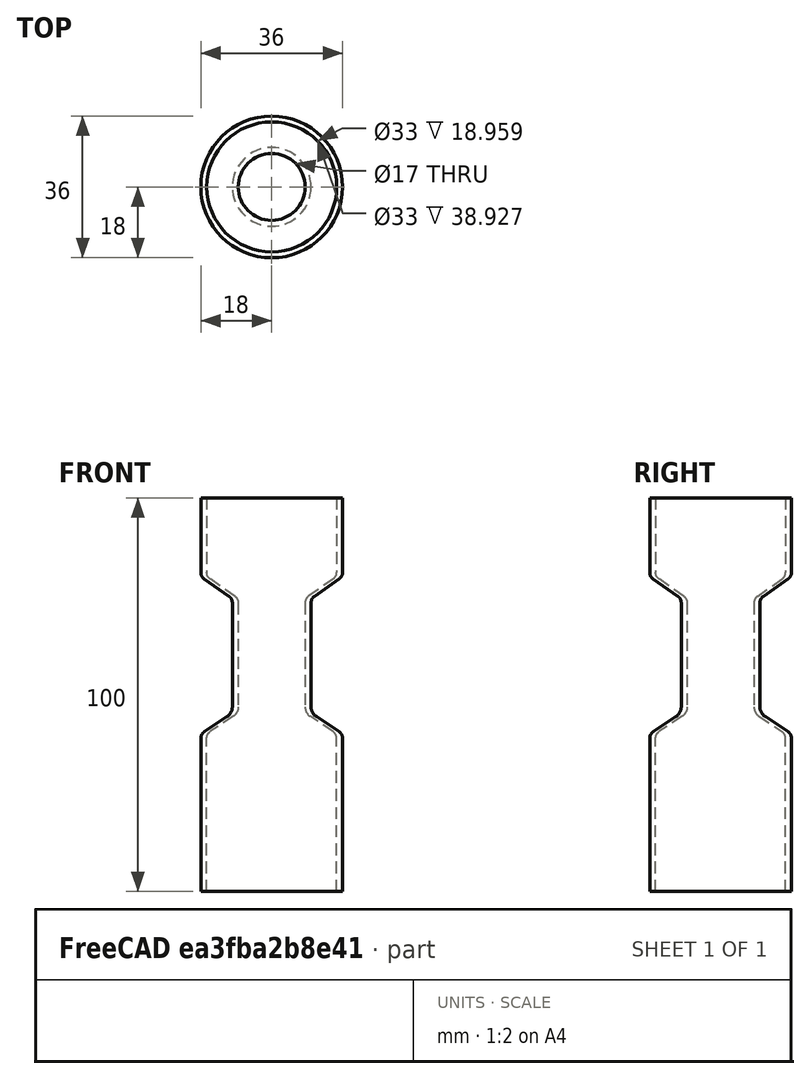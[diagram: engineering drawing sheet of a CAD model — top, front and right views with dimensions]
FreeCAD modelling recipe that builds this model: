
FCSTD DOCUMENT  (FreeCAD 0.20R29177 (Git))
Label: IntestineV3
License: All rights reserved
LicenseURL: http://en.wikipedia.org/wiki/All_rights_reserved
objects: Sketcher::SketchObject×1, Part::Revolution×1
note: 2 computed .brp shape members not serialized (recipe doc carries the construction recipe); baked Part::Feature solids carry a one-line shape summary decoded from their .brp

FEATURE [Sketcher::SketchObject] Sketch
  FullyConstrained = false
  Placement = pos=(0,0,0) rot=(1,0,0;1.5708rad)
  sketch-geometry (28):
    g0: LineSegment StartX=18 StartY=0 StartZ=0 EndX=18 EndY=38.9273 EndZ=0
    g1: LineSegment StartX=18 StartY=100 StartZ=0 EndX=16.5 EndY=100 EndZ=0
    g2: LineSegment StartX=16.5 StartY=100 StartZ=0 EndX=16.5 EndY=81.041 EndZ=0
    g3: LineSegment StartX=18 StartY=0 StartZ=0 EndX=16.5 EndY=0 EndZ=0
    g4: LineSegment StartX=16.5 StartY=0 StartZ=0 EndX=16.5 EndY=38.9273 EndZ=0
    g5: LineSegment StartX=10 StartY=73.3558 StartZ=0 EndX=10 EndY=46.9213 EndZ=0
    g6: LineSegment StartX=8.5 StartY=73.3558 StartZ=0 EndX=8.5 EndY=46.9213 EndZ=0
    g7: LineSegment StartX=15.6474 StartY=79.4028 StartZ=0 EndX=9.35264 EndY=74.994 EndZ=0
    g8: LineSegment StartX=10.8526 StartY=74.994 StartZ=0 EndX=17.1474 EndY=79.4028 EndZ=0
    g9: LineSegment StartX=15.6064 StartY=40.5934 StartZ=0 EndX=9.84046 EndY=44.4221 EndZ=0
    g10: LineSegment StartX=11.3405 StartY=44.4221 StartZ=0 EndX=17.1064 EndY=40.5934 EndZ=0
    g11: LineSegment StartX=18 StartY=81.041 StartZ=0 EndX=18 EndY=100 EndZ=0
    g12: ArcOfCircle CenterX=16 CenterY=81.041 CenterZ=0 NormalX=0 NormalY=0 NormalZ=1 AngleXU=0 Radius=2 StartAngle=5.32338 EndAngle=6.28319
    g13: GeomPoint X=18 Y=80 Z=0
    g14: ArcOfCircle CenterX=14.5 CenterY=81.041 CenterZ=0 NormalX=0 NormalY=0 NormalZ=1 AngleXU=0 Radius=2 StartAngle=5.32338 EndAngle=6.28319
    g15: GeomPoint X=16.5 Y=80 Z=0
    g16: ArcOfCircle CenterX=12 CenterY=73.3558 CenterZ=0 NormalX=0 NormalY=0 NormalZ=1 AngleXU=0 Radius=2 StartAngle=2.18179 EndAngle=3.14159
    g17: GeomPoint X=10 Y=74.3968 Z=0
    g18: ArcOfCircle CenterX=10.5 CenterY=73.3558 CenterZ=0 NormalX=0 NormalY=0 NormalZ=1 AngleXU=0 Radius=2 StartAngle=2.18179 EndAngle=3.14159
    g19: GeomPoint X=8.5 Y=74.3968 Z=0
    g20: ArcOfCircle CenterX=11.5 CenterY=46.9213 CenterZ=0 NormalX=0 NormalY=0 NormalZ=1 AngleXU=0 Radius=3 StartAngle=3.14159 EndAngle=4.12621
    g21: GeomPoint X=8.5 Y=45.3123 Z=0
    g22: ArcOfCircle CenterX=13 CenterY=46.9213 CenterZ=0 NormalX=0 NormalY=0 NormalZ=1 AngleXU=0 Radius=3 StartAngle=3.14159 EndAngle=4.12621
    g23: GeomPoint X=10 Y=45.3123 Z=0
    g24: ArcOfCircle CenterX=14.5 CenterY=38.9273 CenterZ=0 NormalX=0 NormalY=0 NormalZ=1 AngleXU=0 Radius=2 StartAngle=0 EndAngle=0.98462
    g25: GeomPoint X=16.5 Y=40 Z=0
    g26: ArcOfCircle CenterX=16 CenterY=38.9273 CenterZ=0 NormalX=0 NormalY=0 NormalZ=1 AngleXU=0 Radius=2 StartAngle=1.4e-15 EndAngle=0.98462
    g27: GeomPoint X=18 Y=40 Z=0
  constraints (66):
    c: Vertical(g0)
    c: DistanceY(g0,g11) = 100
    c: Coincident(g1,g11)
    c: Horizontal(g1)
    c: DistanceX(g1,g1) = 1.5
    c: Coincident(g2,g1)
    c: Vertical(g2)
    c: DistanceY(g15,g2) = 20
    c: Coincident(g3,g0)
    c: PointOnObject(g3,g-1)
    c: Horizontal(g3)
    c: DistanceX(g3,g3) = 1.5
    c: Coincident(g4,g3)
    c: Vertical(g4)
    c: DistanceX(g-1,g0) = 18
    c: Vertical(g5)
    c: Vertical(g6)
    c: DistanceX(g-1,g17) = 10
    c: DistanceX(g-1,g19) = 8.5
    c: Parallel(g11,g2)
    c: DistanceX(g-1,g1) = 18
    c: PointOnObject(g13,g11)
    c: PointOnObject(g13,g8)
    c: Tangent(g11,g12) = -1.5708
    c: Tangent(g8,g12) = -1.5708
    c: PointOnObject(g15,g2)
    c: PointOnObject(g15,g7)
    c: Tangent(g2,g14) = 1.5708
    c: Tangent(g7,g14) = 1.5708
    c: PointOnObject(g17,g8)
    c: PointOnObject(g17,g5)
    c: Tangent(g8,g16) = 1.5708
    c: Tangent(g5,g16) = -1.5708
    c: PointOnObject(g19,g7)
    c: PointOnObject(g19,g6)
    c: Tangent(g7,g18) = -1.5708
    c: Tangent(g6,g18) = -1.5708
    c: PointOnObject(g21,g9)
    c: PointOnObject(g21,g6)
    c: Tangent(g9,g20) = 1.5708
    c: Tangent(g6,g20) = -1.5708
    c: PointOnObject(g23,g5)
    c: PointOnObject(g23,g10)
    c: Tangent(g5,g22) = -1.5708
    c: Tangent(g10,g22) = -1.5708
    c: PointOnObject(g25,g4)
    c: PointOnObject(g25,g9)
    c: Tangent(g4,g24) = -1.5708
    c: Tangent(g9,g24) = -1.5708
    c: PointOnObject(g27,g10)
    c: PointOnObject(g27,g0)
    c: Tangent(g10,g26) = 1.5708
    c: Tangent(g0,g26) = -1.5708
    c: DistanceY(g13,g15) = 0
    c: DistanceY(g-1,g27) = 40
    c: Equal(g10,g9)
    c: Radius(g14) = 2
    c: Radius(g12) = 2
    c: Radius(g16) = 2
    c: Radius(g18) = 2
    c: Radius(g22) = 3
    c: Radius(g20) = 3
    c: Radius(g24) = 2
    c: Radius(g26) = 2
    c: DistanceY(g27,g25) = 0
    c: Equal(g8,g7)
FEATURE [Part::Revolution] Revolve
  Angle = 360
  Axis = (0,0,1)
  Base = (0,0,0)
  FaceMakerClass = Part::FaceMakerBullseye
  Solid = true
  Source = -> Sketch
  Symmetric = false
